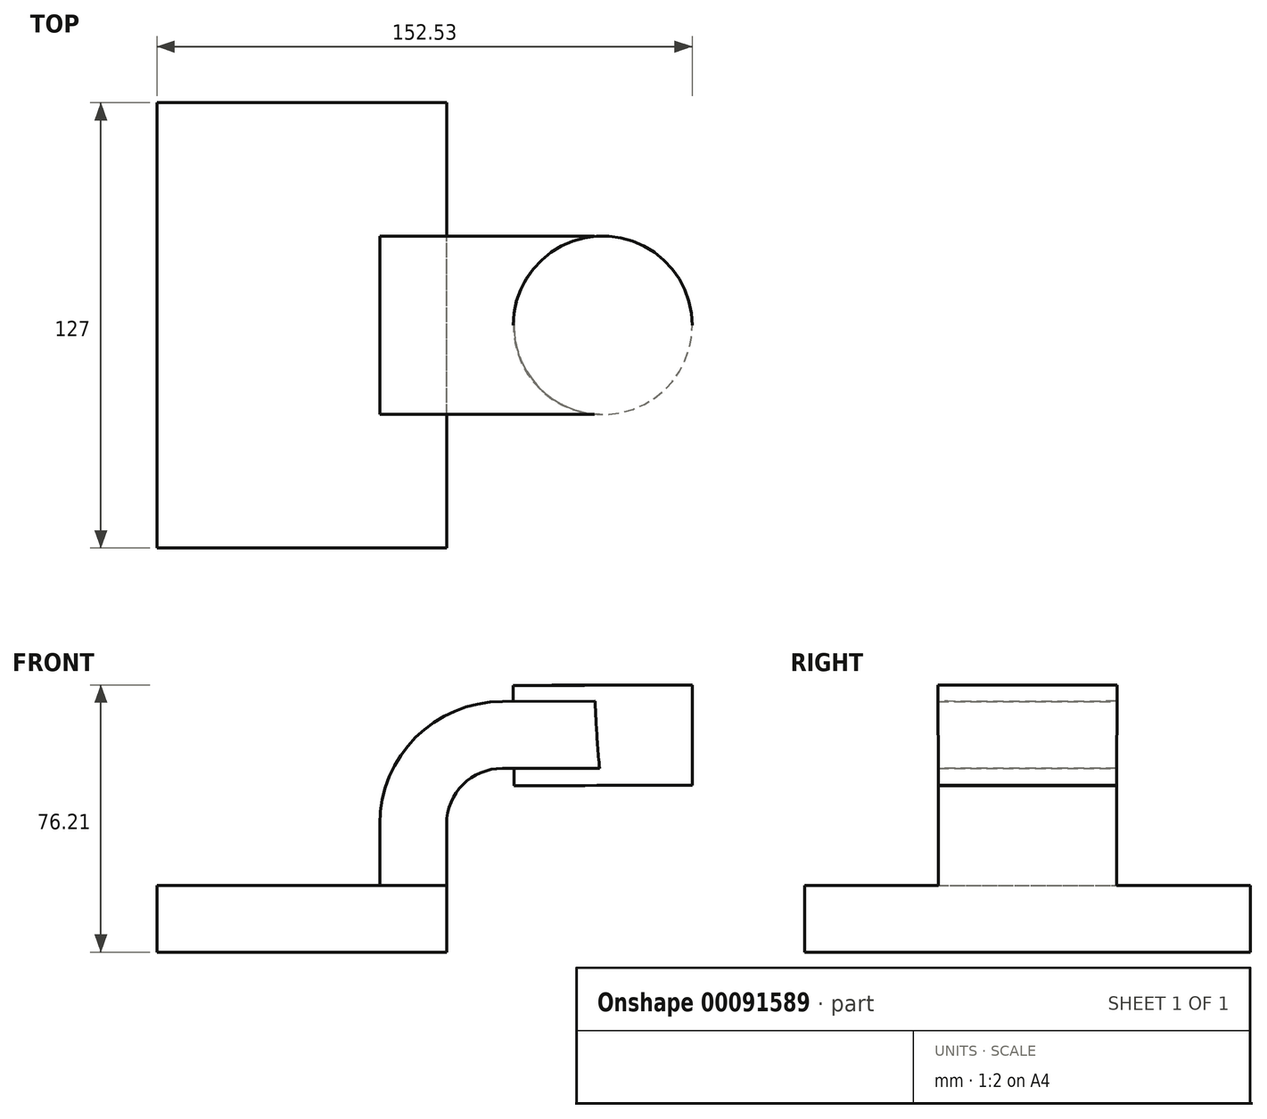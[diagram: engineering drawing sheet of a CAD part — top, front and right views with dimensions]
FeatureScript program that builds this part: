
annotation { "Feature Type Name" : "Feature", "Feature Type Description" : "" }
export const myFeature = defineFeature(function(context is Context, id is Id, definition is map)
    precondition{}
    {
        {
            var Q0;
            Q0=qCreatedBy(makeId("Front.planeOp"),FACE);
            var sketch = newSketch(context, id + "F0", { "sketchPlane" : qUnion([Q0])});
            skLineSegment(sketch, "E0.bottom", {"start": v(41.28, -9.52) * mm, "end": v(-41.27, -9.53) * mm});
            skLineSegment(sketch, "E0.top", {"start": v(41.27, 9.53) * mm, "end": v(-41.28, 9.53) * mm});
            skLineSegment(sketch, "E0.left", {"start": v(41.28, -9.52) * mm, "end": v(41.28, 9.53) * mm});
            skLineSegment(sketch, "E0.right", {"start": v(-41.27, -9.53) * mm, "end": v(-41.28, 9.52) * mm});
            skPoint(sketch, "E0.middle", {"position": v(0, 0) * mm});
            skLineSegment(sketch, "E1.bottom", {"start": v(111.25, 38.1) * mm, "end": v(60.45, 38.1) * mm});
            skLineSegment(sketch, "E1.top", {"start": v(111.25, 66.68) * mm, "end": v(60.45, 66.68) * mm});
            skLineSegment(sketch, "E1.left", {"start": v(111.25, 38.1) * mm, "end": v(111.25, 66.67) * mm});
            skLineSegment(sketch, "E1.right", {"start": v(60.45, 38.1) * mm, "end": v(60.45, 66.67) * mm});
            skPoint(sketch, "E1.middle", {"position": v(85.85, 52.39) * mm});
            skLineSegment(sketch, "E2", {"start": v(41.27, 9.53) * mm, "end": v(41.27, 27) * mm});
            skArc(sketch, "E3", {"start": v(41.27, 27) * mm, "mid": v(45.92, 38.23) * mm, "end": v(57.15, 42.88) * mm});
            skArc(sketch, "E4.1", {"start": v(22.23, 27) * mm, "mid": v(32.45, 51.7) * mm, "end": v(57.15, 61.93) * mm});
            skLineSegment(sketch, "E4.2", {"start": v(22.22, 9.53) * mm, "end": v(22.22, 27) * mm});
            skLineSegment(sketch, "E5", {"start": v(57.15, 42.88) * mm, "end": v(85.85, 42.88) * mm});
            skFitSpline(sketch, "E6", {"points": [v(-41.28, 9.53) * mm, v(57.15, 61.93) * mm], "startDerivative": vector(0.09, 97.98) * mm, "endDerivative": vector(147.34, -1.84) * mm});
            skPoint(sketch, "E7", {"position": v(85.85, 38.1) * mm});
            skLineSegment(sketch, "E8", {"start": v(85.74, 66.68) * mm, "end": v(85.85, 38.1) * mm});
            skLineSegment(sketch, "E9", {"start": v(57.15, 61.93) * mm, "end": v(94.5, 62.07) * mm});
            skSolve(sketch);
        }
        {
            var Q0;
            Q0=makeQuery(id+"F0.imprint","IMPRINT",FACE,{"disambiguationData":[TD([[makeQuery(id+"F0.imprint","IMPRINT",EDGE,{"derivedFrom":sQuery(id+"F0.wireOp",EDGE,"E0.bottom")}),-1.0]])]});
            extrude(context, id + "F1", {"entities" : qUnion([Q0]), "endBound" : BoundingType.SYMMETRIC, "depth" : 127 * mm});
        }
        {
            var Q0;
            {var subQ4=sQuery(id+"F0.wireOp",EDGE,"E2");Q0=makeQuery(id+"F0.imprint","IMPRINT",FACE,{"disambiguationData":[TD([[makeQuery(id+"F0.imprint","IMPRINT",EDGE,{"derivedFrom":subQ4}),1.0]])]});}
            var Q1;
            {var subQ0=sQuery(id+"F0.wireOp",EDGE,"E5");var subQ1=sQuery(id+"F0.wireOp",EDGE,"E1.right");var subQ2=makeQuery(id+"F0.imprint","INTERSECT",VERTEX,{"derivedFrom":[subQ1,subQ0]});Q1=makeQuery(id+"F0.imprint","IMPRINT",FACE,{"disambiguationData":[TD([[makeQuery(id+"F0.imprint","IMPRINT",EDGE,{"disambiguationData":[TD([[subQ2,-1.0]])],"derivedFrom":subQ1}),-1.0]])]});}
            extrude(context, id + "F2", {"entities" : qUnion([Q0, Q1]), "operationType" : NewBodyOperationType.ADD, "endBound" : BoundingType.SYMMETRIC, "depth" : 50.8 * mm});
        }
        {
            var Q0;
            Q0=makeQuery(id+"F0.imprint","IMPRINT",FACE,{"disambiguationData":[TD([[makeQuery(id+"F0.imprint","IMPRINT",EDGE,{"derivedFrom":sQuery(id+"F0.wireOp",EDGE,"E4.1")}),1.0]])]});
            extrude(context, id + "F3", {"entities" : qUnion([Q0]), "operationType" : NewBodyOperationType.ADD, "endBound" : BoundingType.SYMMETRIC, "depth" : 25.4 * mm});
        }
        {
            var Q0;
            {var subQ0=sQuery(id+"F0.wireOp",EDGE,"E1.left");Q0=makeQuery(id+"F0.imprint","IMPRINT",FACE,{"disambiguationData":[TD([[makeQuery(id+"F0.imprint","IMPRINT",EDGE,{"derivedFrom":subQ0}),1.0]])]});}
            var Q1;
            Q1=sQuery(id+"F0.wireOp",EDGE,"E8");
            revolve(context, id + "F4", {"operationType" : NewBodyOperationType.ADD, "entities" : qUnion([Q0]), "axis" : qUnion([Q1]), "revolveType" : RevolveType.FULL});
        }
    });
